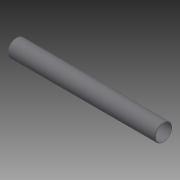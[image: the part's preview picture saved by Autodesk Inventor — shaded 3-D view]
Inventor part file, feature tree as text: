
AUTODESK INVENTOR PART (.ipt)
format: ipt  version: 2014 (Build 180170000, 170)  size: 135,168 bytes
history: native  units: in
note: dims shown in document units (in); Inventor stores cm internally (conversion verified against a paired STEP export)
features: other x42, revolve x1, sketch x1
ambient origin geometry x8: Origin, YZ Plane, XZ Plane, XY Plane, X Axis, Y Axis, Z Axis, Center Point
bodies: Solid1 (feature_tree)
feature tree (44):
  revolve  "Revolution1"  [1 undecoded]
  other  "cp1_XY"
  other  "cp1_YZ"
  other  "cp1_ZX"
  other  "cp1_X"
  other  "cp1_Y"
  other  "cp1_Z"
  other  "cp1_Center"
  other  "cp2_XY"
  other  "cp2_YZ"
  other  "cp2_ZX"
  other  "cp2_X"
  other  "cp2_Y"
  other  "cp2_Z"
  other  "cp2_Center"
  other  "cp3_XY"
  other  "cp3_YZ"
  other  "cp3_ZX"
  other  "cp3_X"
  other  "cp3_Y"
  other  "cp3_Z"
  other  "cp3_Center"
  other  "cp4_XY"
  other  "cp4_YZ"
  other  "cp4_ZX"
  other  "cp4_X"
  other  "cp4_Y"
  other  "cp4_Z"
  other  "cp4_Center"
  other  "tube_front_XY"
  other  "tube_front_YZ"
  other  "tube_front_ZX"
  other  "tube_front_X"
  other  "tube_front_Y"
  other  "tube_front_Z"
  other  "tube_front_Center"
  other  "tube_rear_XY"
  other  "tube_rear_YZ"
  other  "tube_rear_ZX"
  other  "tube_rear_X"
  other  "tube_rear_Y"
  other  "tube_rear_Z"
  other  "tube_rear_Center"
  sketch  "Sketch_1"  dims[d0=360.0deg]
note: 1 required parameter value undecoded (feature->parameter linkage not recoverable at this tier; creation-order binding heuristic only, values carry confidence <= 0.55)
